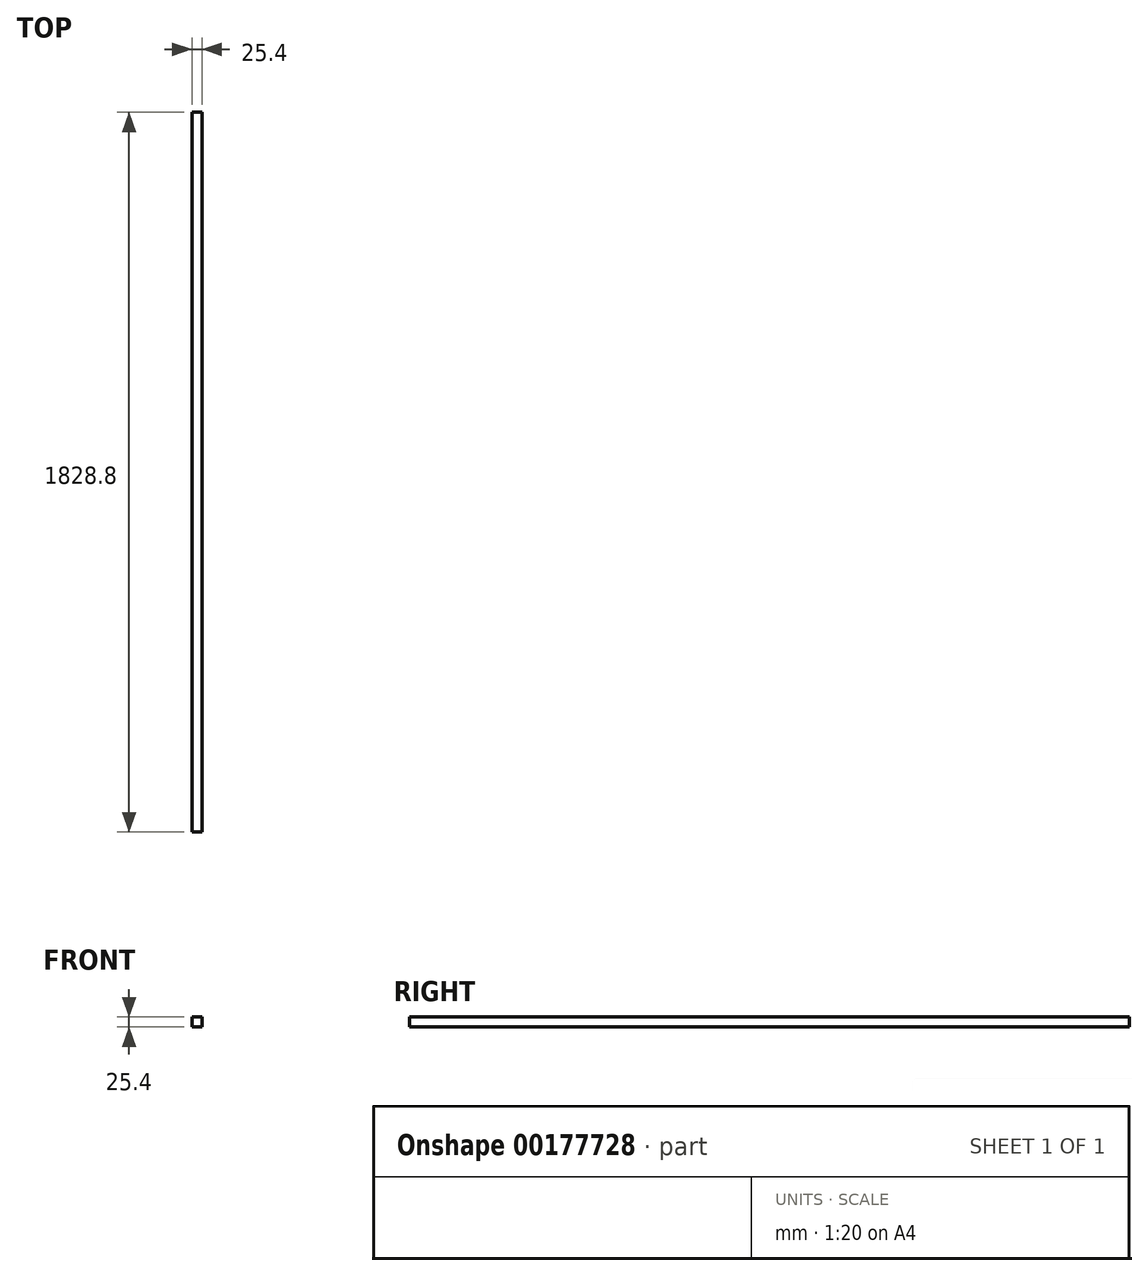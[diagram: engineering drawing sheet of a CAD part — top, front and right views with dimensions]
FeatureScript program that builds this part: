
annotation { "Feature Type Name" : "Feature", "Feature Type Description" : "" }
export const myFeature = defineFeature(function(context is Context, id is Id, definition is map)
    precondition{}
    {
        {
            var Q0;
            Q0=qCreatedBy(makeId("Front.planeOp"),FACE);
            var sketch = newSketch(context, id + "F0", { "sketchPlane" : qUnion([Q0])});
            skLineSegment(sketch, "E0.bottom", {"start": v(0, 25.4) * mm, "end": v(25.4, 25.4) * mm});
            skLineSegment(sketch, "E0.top", {"start": v(0, 0) * mm, "end": v(25.4, 0) * mm});
            skLineSegment(sketch, "E0.left", {"start": v(0, 25.4) * mm, "end": v(0, 0) * mm});
            skLineSegment(sketch, "E0.right", {"start": v(25.4, 25.4) * mm, "end": v(25.4, 0) * mm});
            skSolve(sketch);
        }
        {
            var Q0;
            Q0 = qSketchRegion(id + "F0", true);
            extrude(context, id + "F1", {"entities" : qUnion([Q0]), "endBound" : BoundingType.SYMMETRIC, "depth" : 1828.8 * mm});
        }
    });
